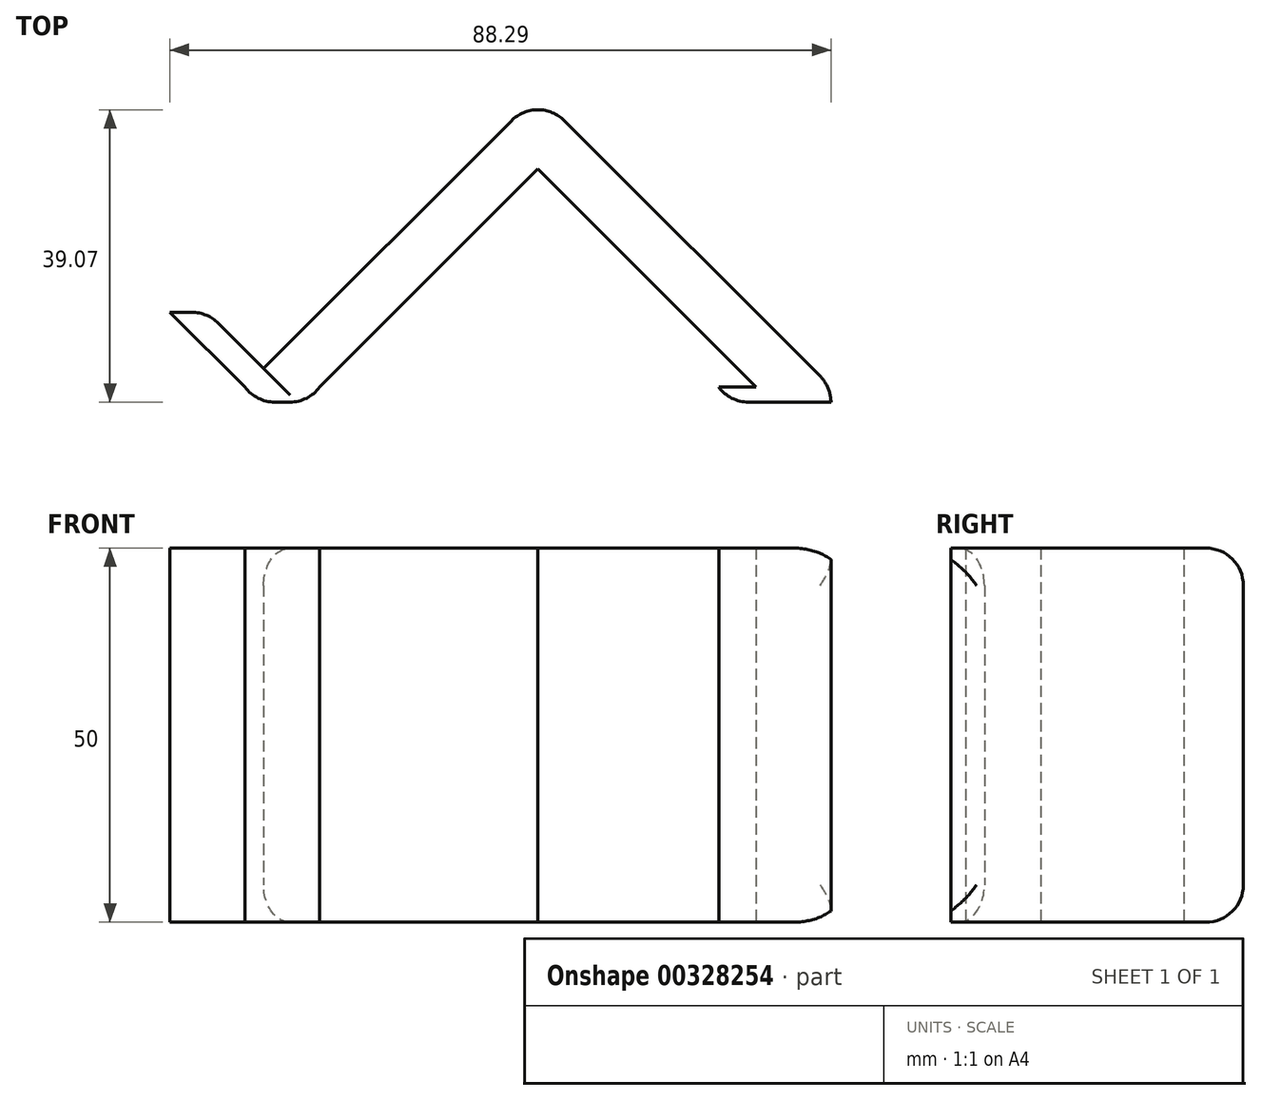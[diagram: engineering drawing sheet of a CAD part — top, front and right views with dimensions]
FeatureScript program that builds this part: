
annotation { "Feature Type Name" : "Feature", "Feature Type Description" : "" }
export const myFeature = defineFeature(function(context is Context, id is Id, definition is map)
    precondition{}
    {
        {
            var Q0;
            Q0=qCreatedBy(makeId("Top.planeOp"),FACE);
            var sketch = newSketch(context, id + "F0", { "sketchPlane" : qUnion([Q0])});
            skLineSegment(sketch, "E0", {"start": v(39.14, 39.14) * mm, "end": v(78.29, 0) * mm});
            skLineSegment(sketch, "E1", {"start": v(39.14, 39.14) * mm, "end": v(2.5, 2.5) * mm});
            skLineSegment(sketch, "E2", {"start": v(39.14, 29.14) * mm, "end": v(10, 0) * mm});
            skLineSegment(sketch, "E3", {"start": v(39.14, 29.14) * mm, "end": v(68.29, 0) * mm});
            skLineSegment(sketch, "E4.bottom", {"start": v(68.29, 0) * mm, "end": v(63.29, 0) * mm});
            skLineSegment(sketch, "E4.top", {"start": v(78.29, -2) * mm, "end": v(63.29, -2) * mm});
            skLineSegment(sketch, "E4.left", {"start": v(78.29, 0) * mm, "end": v(78.29, -2) * mm});
            skLineSegment(sketch, "E4.right", {"start": v(63.29, 0) * mm, "end": v(63.29, -2) * mm});
            skLineSegment(sketch, "E5", {"start": v(-10, 10) * mm, "end": v(0, 0) * mm});
            skPoint(sketch, "E6.orphan", {"position": v(-10, 0) * mm});
            skLineSegment(sketch, "E7", {"start": v(-5, 10) * mm, "end": v(2.5, 2.5) * mm});
            skPoint(sketch, "E8.orphan", {"position": v(0, 10) * mm});
            skPoint(sketch, "E9.orphan", {"position": v(5, 10) * mm});
            skPoint(sketch, "E10.orphan", {"position": v(-5, 0) * mm});
            skLineSegment(sketch, "E11", {"start": v(-10, 10) * mm, "end": v(-5, 10) * mm});
            skLineSegment(sketch, "E12.top", {"start": v(0, -2) * mm, "end": v(10, -2) * mm});
            skLineSegment(sketch, "E12.left", {"start": v(0, 0) * mm, "end": v(0, -2) * mm});
            skLineSegment(sketch, "E12.right", {"start": v(10, 0) * mm, "end": v(10, -2) * mm});
            skSolve(sketch);
        }
        {
            var Q0;
            Q0=makeQuery(id+"F0.imprint","IMPRINT",FACE,{"disambiguationData":[TD([[makeQuery(id+"F0.imprint","IMPRINT",EDGE,{"derivedFrom":sQuery(id+"F0.wireOp",EDGE,"E0")}),-1.0]])]});
            extrude(context, id + "F1", {"entities" : qUnion([Q0]), "depth" : 50 * mm});
        }
        {
            var Q0;
            Q0=makeQuery(id+"F1.opExtrude","SWEPT_EDGE",EDGE,{"disambiguationData":[OSD([sQuery(id+"F0.wireOp",EDGE,"E7"),sQuery(id+"F0.wireOp",EDGE,"E11")])]});
            var Q1;
            Q1=makeQuery(id+"F1.opExtrude","SWEPT_EDGE",EDGE,{"disambiguationData":[OSD([sQuery(id+"F0.wireOp",EDGE,"E0"),sQuery(id+"F0.wireOp",EDGE,"E1")])]});
            var Q2;
            Q2=makeQuery(id+"F1.opExtrude","SWEPT_EDGE",EDGE,{"disambiguationData":[OSD([sQuery(id+"F0.wireOp",EDGE,"E12.top"),sQuery(id+"F0.wireOp",EDGE,"E12.left")])]});
            var Q3;
            Q3=makeQuery(id+"F1.opExtrude","SWEPT_EDGE",EDGE,{"disambiguationData":[OSD([sQuery(id+"F0.wireOp",EDGE,"E12.top"),sQuery(id+"F0.wireOp",EDGE,"E12.right")])]});
            var Q4;
            Q4=makeQuery(id+"F1.opExtrude","SWEPT_EDGE",EDGE,{"disambiguationData":[OSD([sQuery(id+"F0.wireOp",EDGE,"E0"),sQuery(id+"F0.wireOp",EDGE,"E4.left")])]});
            var Q5;
            Q5=makeQuery(id+"F1.opExtrude","SWEPT_EDGE",EDGE,{"disambiguationData":[OSD([sQuery(id+"F0.wireOp",EDGE,"E4.top"),sQuery(id+"F0.wireOp",EDGE,"E4.right")])]});
            var Q6;
            Q6=makeQuery(id+"F1.opExtrude","CAP_EDGE",EDGE,{"disambiguationData":[OSD([sQuery(id+"F0.wireOp",EDGE,"E0")])],"isStart":true});
            var Q7;
            Q7=makeQuery(id+"F1.opExtrude","CAP_EDGE",EDGE,{"disambiguationData":[OSD([sQuery(id+"F0.wireOp",EDGE,"E1")])],"isStart":true});
            var Q8;
            Q8=makeQuery(id+"F1.opExtrude","CAP_EDGE",EDGE,{"disambiguationData":[OSD([sQuery(id+"F0.wireOp",EDGE,"E1")])],"isStart":false});
            var Q9;
            Q9=makeQuery(id+"F1.opExtrude","CAP_EDGE",EDGE,{"disambiguationData":[OSD([sQuery(id+"F0.wireOp",EDGE,"E0")])],"isStart":false});
            fillet(context, id + "F2", {"entities" : qUnion([Q0, Q1, Q2, Q3, Q4, Q5, Q6, Q7, Q8, Q9]), "radius" : 5 * mm, "tangentPropagation" : true, "allowEdgeOverflow" : false});
        }
    });
